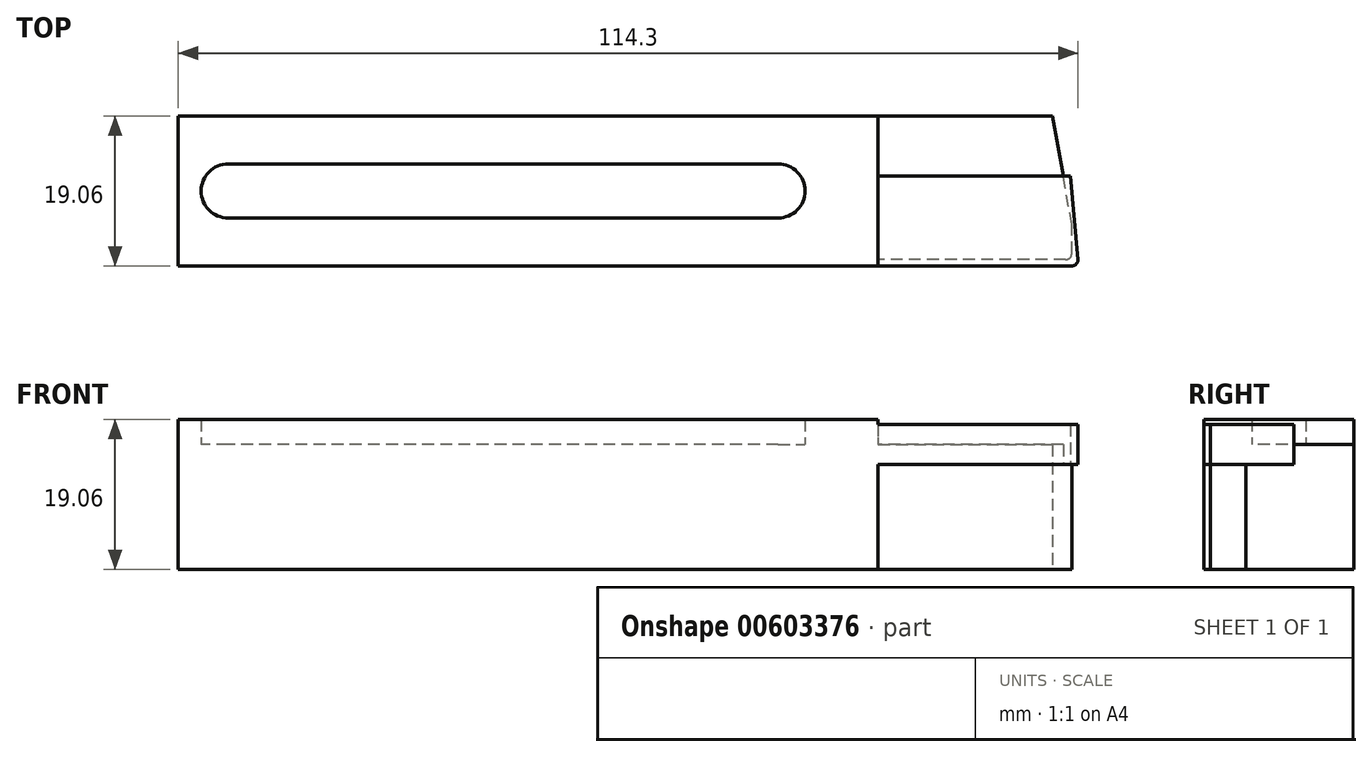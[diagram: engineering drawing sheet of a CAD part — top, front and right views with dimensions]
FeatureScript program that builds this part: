
annotation { "Feature Type Name" : "Feature", "Feature Type Description" : "" }
export const myFeature = defineFeature(function(context is Context, id is Id, definition is map)
    precondition{}
    {
        {
            var Q0;
            Q0=qCreatedBy(makeId("Top.planeOp"),FACE);
            var sketch = newSketch(context, id + "F0", { "sketchPlane" : qUnion([Q0])});
            skLineSegment(sketch, "E0.bottom", {"start": v(-57.15, -9.53) * mm, "end": v(56.36, -9.53) * mm});
            skLineSegment(sketch, "E0.top", {"start": v(-57.15, 9.53) * mm, "end": v(53.93, 9.53) * mm});
            skLineSegment(sketch, "E0.left", {"start": v(-57.15, -9.53) * mm, "end": v(-57.15, 9.53) * mm});
            skPoint(sketch, "E0.middle", {"position": v(0, 0) * mm});
            skLineSegment(sketch, "E1", {"start": v(31.75, 9.53) * mm, "end": v(31.75, -9.53) * mm});
            skPoint(sketch, "E2.visualSharp", {"position": v(57.15, -9.53) * mm});
            skArc(sketch, "E2.filletArc", {"start": v(56.36, -9.53) * mm, "mid": v(56.92, -9.3) * mm, "end": v(57.15, -8.73) * mm});
            skLineSegment(sketch, "E3", {"start": v(57.15, -8.73) * mm, "end": v(56.22, 1.9) * mm});
            skLineSegment(sketch, "E4", {"start": v(57.15, -8.73) * mm, "end": v(53.93, 9.53) * mm});
            skLineSegment(sketch, "E5", {"start": v(31.75, 1.9) * mm, "end": v(56.22, 1.9) * mm});
            skPoint(sketch, "E6.orphan", {"position": v(57.15, 9.53) * mm});
            skLineSegment(sketch, "E7", {"start": v(55.56, -8.73) * mm, "end": v(31.75, -8.73) * mm});
            skLineSegment(sketch, "E8", {"start": v(56.36, -7.94) * mm, "end": v(56.36, -4.23) * mm});
            skArc(sketch, "E9.filletArc", {"start": v(55.56, -8.73) * mm, "mid": v(56.12, -8.5) * mm, "end": v(56.36, -7.94) * mm});
            skCircle(sketch, "E10", {"center": v(-50.8, 0) * mm, "radius": 3.43 * mm});
            skCircle(sketch, "E11", {"center": v(19.05, 0) * mm, "radius": 3.43 * mm});
            skLineSegment(sketch, "E12", {"start": v(19.05, -3.43) * mm, "end": v(-50.8, -3.43) * mm});
            skLineSegment(sketch, "E13", {"start": v(19.05, 3.43) * mm, "end": v(-50.8, 3.43) * mm});
            skSolve(sketch);
        }
        {
            var Q0;
            {var subQ0=sQuery(id+"F0.wireOp",EDGE,"E0.left");Q0=makeQuery(id+"F0.imprint","IMPRINT",FACE,{"disambiguationData":[TD([[makeQuery(id+"F0.imprint","IMPRINT",EDGE,{"derivedFrom":subQ0}),-1.0]])]});}
            var Q1;
            {var subQ0=sQuery(id+"F0.wireOp",EDGE,"E7");Q1=makeQuery(id+"F0.imprint","IMPRINT",FACE,{"disambiguationData":[TD([[makeQuery(id+"F0.imprint","IMPRINT",EDGE,{"derivedFrom":subQ0}),-1.0]])]});}
            var Q2;
            {var subQ0=sQuery(id+"F0.wireOp",EDGE,"E4");var subQ1=sQuery(id+"F0.wireOp",EDGE,"E0.top");var subQ2=makeQuery(id+"F0.imprint","INTERSECT",VERTEX,{"derivedFrom":[subQ1,subQ0]});Q2=makeQuery(id+"F0.imprint","IMPRINT",FACE,{"disambiguationData":[TD([[makeQuery(id+"F0.imprint","IMPRINT",EDGE,{"disambiguationData":[TD([[subQ2,1.0]])],"derivedFrom":subQ1}),-1.0]])]});}
            var Q3;
            {var subQ0=sQuery(id+"F0.wireOp",EDGE,"E10");var subQ1=makeQuery(id+"F0.imprint","INTERSECT",VERTEX,{"derivedFrom":[subQ0,sQuery(id+"F0.wireOp",EDGE,"E12")]});Q3=makeQuery(id+"F0.imprint","IMPRINT",FACE,{"disambiguationData":[TD([[makeQuery(id+"F0.imprint","IMPRINT",EDGE,{"disambiguationData":[TD([[subQ1,1.0]])],"derivedFrom":subQ0}),1.0]])]});}
            var Q4;
            {var subQ0=sQuery(id+"F0.wireOp",EDGE,"E12");Q4=makeQuery(id+"F0.imprint","IMPRINT",FACE,{"disambiguationData":[TD([[makeQuery(id+"F0.imprint","IMPRINT",EDGE,{"derivedFrom":subQ0}),-1.0]])]});}
            var Q5;
            {var subQ0=sQuery(id+"F0.wireOp",EDGE,"E11");var subQ1=makeQuery(id+"F0.imprint","INTERSECT",VERTEX,{"derivedFrom":[subQ0,sQuery(id+"F0.wireOp",EDGE,"E12")]});Q5=makeQuery(id+"F0.imprint","IMPRINT",FACE,{"disambiguationData":[TD([[makeQuery(id+"F0.imprint","IMPRINT",EDGE,{"disambiguationData":[TD([[subQ1,1.0]])],"derivedFrom":subQ0}),1.0]])]});}
            extrude(context, id + "F1", {"entities" : qUnion([Q0, Q1, Q2, Q3, Q4, Q5]), "endBound" : BoundingType.SYMMETRIC, "depth" : 19.05 * mm, "offsetDistance" : 25.4 * mm});
        }
        {
            var Q0;
            {var subQ0=sQuery(id+"F0.wireOp",EDGE,"E7");Q0=makeQuery(id+"F0.imprint","IMPRINT",FACE,{"disambiguationData":[TD([[makeQuery(id+"F0.imprint","IMPRINT",EDGE,{"derivedFrom":subQ0}),-1.0]])]});}
            var Q1;
            {var subQ0=sQuery(id+"F0.wireOp",EDGE,"E4");var subQ1=sQuery(id+"F0.wireOp",EDGE,"E0.top");var subQ2=makeQuery(id+"F0.imprint","INTERSECT",VERTEX,{"derivedFrom":[subQ1,subQ0]});Q1=makeQuery(id+"F0.imprint","IMPRINT",FACE,{"disambiguationData":[TD([[makeQuery(id+"F0.imprint","IMPRINT",EDGE,{"disambiguationData":[TD([[subQ2,1.0]])],"derivedFrom":subQ1}),-1.0]])]});}
            var Q2;
            {var subQ0=sQuery(id+"F0.wireOp",EDGE,"E10");var subQ1=makeQuery(id+"F0.imprint","INTERSECT",VERTEX,{"derivedFrom":[subQ0,sQuery(id+"F0.wireOp",EDGE,"E12")]});Q2=makeQuery(id+"F0.imprint","IMPRINT",FACE,{"disambiguationData":[TD([[makeQuery(id+"F0.imprint","IMPRINT",EDGE,{"disambiguationData":[TD([[subQ1,1.0]])],"derivedFrom":subQ0}),1.0]])]});}
            var Q3;
            {var subQ0=sQuery(id+"F0.wireOp",EDGE,"E12");Q3=makeQuery(id+"F0.imprint","IMPRINT",FACE,{"disambiguationData":[TD([[makeQuery(id+"F0.imprint","IMPRINT",EDGE,{"derivedFrom":subQ0}),-1.0]])]});}
            var Q4;
            {var subQ0=sQuery(id+"F0.wireOp",EDGE,"E11");var subQ1=makeQuery(id+"F0.imprint","INTERSECT",VERTEX,{"derivedFrom":[subQ0,sQuery(id+"F0.wireOp",EDGE,"E12")]});Q4=makeQuery(id+"F0.imprint","IMPRINT",FACE,{"disambiguationData":[TD([[makeQuery(id+"F0.imprint","IMPRINT",EDGE,{"disambiguationData":[TD([[subQ1,1.0]])],"derivedFrom":subQ0}),1.0]])]});}
            extrude(context, id + "F2", {"entities" : qUnion([Q0, Q1, Q2, Q3, Q4]), "operationType" : NewBodyOperationType.REMOVE, "depth" : 12.7 * mm, "offsetDistance" : 5.08 * mm, "offsetOppositeDirection" : true, "hasSecondDirection" : true, "secondDirectionOppositeDirection" : false, "secondDirectionDepth" : 6.35 * mm});
        }
        {
            var Q0;
            {var subQ1=sQuery(id+"F0.wireOp",EDGE,"E2.filletArc");Q0=makeQuery(id+"F0.imprint","IMPRINT",FACE,{"disambiguationData":[TD([[makeQuery(id+"F0.imprint","IMPRINT",EDGE,{"derivedFrom":subQ1}),1.0]])]});}
            var Q1;
            {var subQ0=sQuery(id+"F0.wireOp",EDGE,"E7");Q1=makeQuery(id+"F0.imprint","IMPRINT",FACE,{"disambiguationData":[TD([[makeQuery(id+"F0.imprint","IMPRINT",EDGE,{"derivedFrom":subQ0}),-1.0]])]});}
            var Q2;
            {var subQ0=sQuery(id+"F0.wireOp",EDGE,"E3");Q2=makeQuery(id+"F0.imprint","IMPRINT",FACE,{"disambiguationData":[TD([[makeQuery(id+"F0.imprint","IMPRINT",EDGE,{"derivedFrom":subQ0}),1.0]])]});}
            extrude(context, id + "F3", {"entities" : qUnion([Q0, Q1, Q2]), "operationType" : NewBodyOperationType.ADD, "depth" : 8.9 * mm, "offsetDistance" : 25.4 * mm, "hasSecondDirection" : true, "secondDirectionOppositeDirection" : false, "secondDirectionDepth" : 3.8 * mm});
        }
    });
